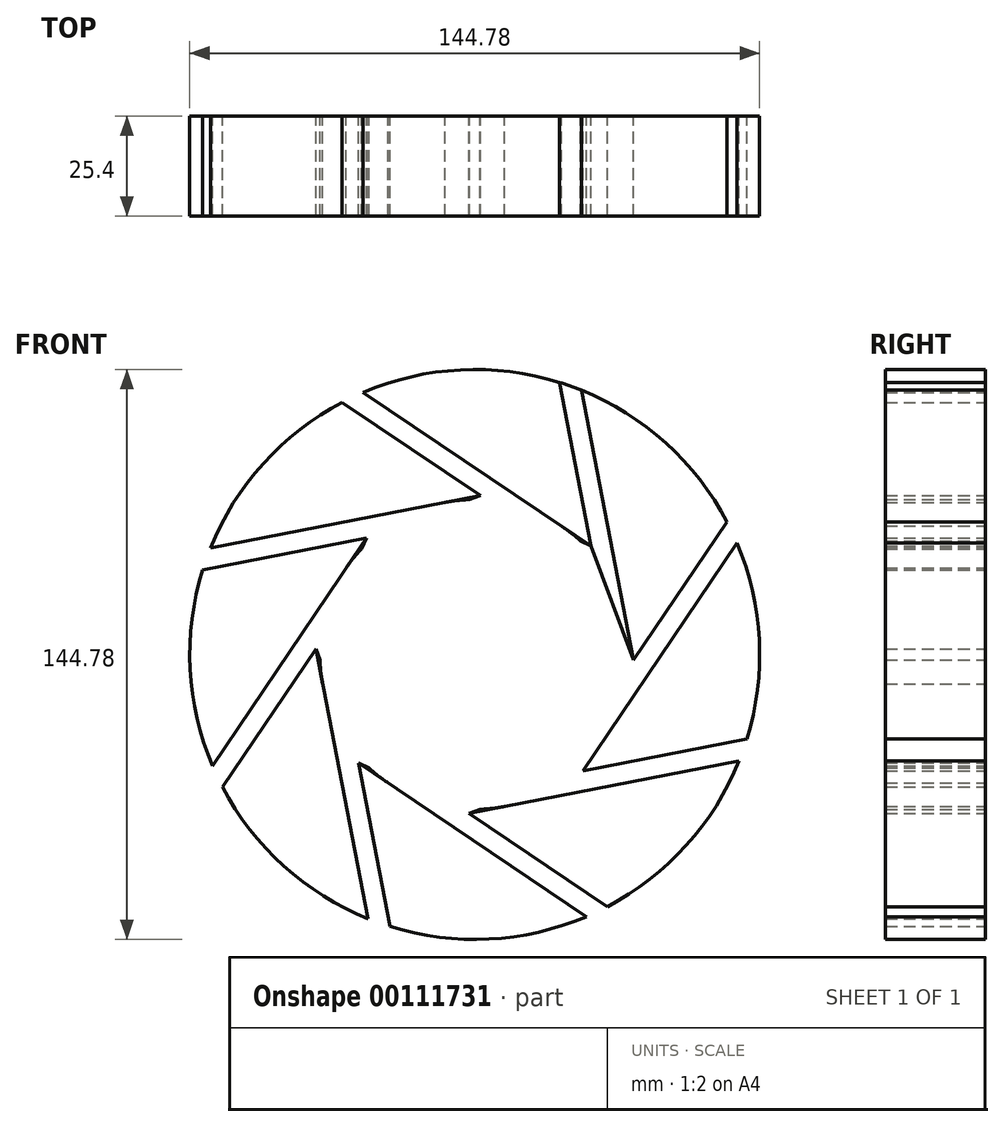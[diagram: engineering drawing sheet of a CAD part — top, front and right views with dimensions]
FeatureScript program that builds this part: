
annotation { "Feature Type Name" : "Feature", "Feature Type Description" : "" }
export const myFeature = defineFeature(function(context is Context, id is Id, definition is map)
    precondition{}
    {
        {
            var Q0;
            Q0=qCreatedBy(makeId("Front.planeOp"),FACE);
            var sketch = newSketch(context, id + "F0", { "sketchPlane" : qUnion([Q0])});
            skCircle(sketch, "E0", {"center": v(0, 0) * mm, "radius": 39.37 * mm});
            skCircle(sketch, "E1", {"center": v(0, 0) * mm, "radius": 72.4 * mm});
            skLineSegment(sketch, "E2", {"start": v(-67.14, 27.06) * mm, "end": v(1.42, 40.38) * mm});
            skLineSegment(sketch, "E3", {"start": v(1.42, 40.38) * mm, "end": v(-33.7, 64.07) * mm});
            skLineSegment(sketch, "E4.1.0", {"start": v(-66.6, -28.35) * mm, "end": v(-27.55, 29.56) * mm});
            skLineSegment(sketch, "E4.1.1", {"start": v(-27.55, 29.56) * mm, "end": v(-69.13, 21.48) * mm});
            skLineSegment(sketch, "E4.2.0", {"start": v(-27.06, -67.14) * mm, "end": v(-40.38, 1.42) * mm});
            skLineSegment(sketch, "E4.2.1", {"start": v(-40.38, 1.42) * mm, "end": v(-64.07, -33.7) * mm});
            skLineSegment(sketch, "E4.3.0", {"start": v(28.35, -66.6) * mm, "end": v(-29.56, -27.55) * mm});
            skLineSegment(sketch, "E4.3.1", {"start": v(-29.56, -27.55) * mm, "end": v(-21.48, -69.13) * mm});
            skLineSegment(sketch, "E4.4.0", {"start": v(67.14, -27.06) * mm, "end": v(-1.42, -40.38) * mm});
            skLineSegment(sketch, "E4.4.1", {"start": v(-1.42, -40.38) * mm, "end": v(33.7, -64.07) * mm});
            skLineSegment(sketch, "E4.5.0", {"start": v(66.6, 28.35) * mm, "end": v(27.55, -29.56) * mm});
            skLineSegment(sketch, "E4.5.1", {"start": v(27.55, -29.56) * mm, "end": v(69.13, -21.48) * mm});
            skLineSegment(sketch, "E4.6.0", {"start": v(27.06, 67.14) * mm, "end": v(40.38, -1.42) * mm});
            skLineSegment(sketch, "E4.6.1", {"start": v(40.38, -1.42) * mm, "end": v(64.07, 33.7) * mm});
            skLineSegment(sketch, "E4.7.0", {"start": v(-28.35, 66.6) * mm, "end": v(29.56, 27.55) * mm});
            skLineSegment(sketch, "E4.7.1", {"start": v(29.56, 27.55) * mm, "end": v(21.48, 69.13) * mm});
            skCircle(sketch, "E5.cCircle", {"center": v(0, 0) * mm, "radius": 40.4 * mm, "construction": true});
            skLineSegment(sketch, "E5.0", {"start": v(1.42, 40.38) * mm, "end": v(29.56, 27.55) * mm});
            skLineSegment(sketch, "E5.1", {"start": v(29.56, 27.55) * mm, "end": v(40.38, -1.42) * mm});
            skLineSegment(sketch, "E5.2", {"start": v(40.38, -1.42) * mm, "end": v(27.55, -29.56) * mm});
            skLineSegment(sketch, "E5.3", {"start": v(27.55, -29.56) * mm, "end": v(-1.42, -40.38) * mm});
            skLineSegment(sketch, "E5.4", {"start": v(-1.42, -40.38) * mm, "end": v(-29.56, -27.55) * mm});
            skLineSegment(sketch, "E5.5", {"start": v(-29.56, -27.55) * mm, "end": v(-40.38, 1.42) * mm});
            skLineSegment(sketch, "E5.6", {"start": v(-40.38, 1.42) * mm, "end": v(-27.55, 29.56) * mm});
            skLineSegment(sketch, "E5.7", {"start": v(-27.55, 29.56) * mm, "end": v(1.42, 40.38) * mm});
            skSolve(sketch);
        }
        {
            var Q0;
            {var subQ3=sQuery(id+"F0.wireOp",EDGE,"E3");Q0=makeQuery(id+"F0.imprint","IMPRINT",FACE,{"disambiguationData":[TD([[makeQuery(id+"F0.imprint","IMPRINT",EDGE,{"derivedFrom":subQ3}),1.0]])]});}
            var Q1;
            {var subQ3=sQuery(id+"F0.wireOp",EDGE,"E4.7.1");Q1=makeQuery(id+"F0.imprint","IMPRINT",FACE,{"disambiguationData":[TD([[makeQuery(id+"F0.imprint","IMPRINT",EDGE,{"derivedFrom":subQ3}),1.0]])]});}
            var Q2;
            {var subQ3=sQuery(id+"F0.wireOp",EDGE,"E4.6.1");Q2=makeQuery(id+"F0.imprint","IMPRINT",FACE,{"disambiguationData":[TD([[makeQuery(id+"F0.imprint","IMPRINT",EDGE,{"derivedFrom":subQ3}),1.0]])]});}
            var Q3;
            {var subQ3=sQuery(id+"F0.wireOp",EDGE,"E4.5.1");Q3=makeQuery(id+"F0.imprint","IMPRINT",FACE,{"disambiguationData":[TD([[makeQuery(id+"F0.imprint","IMPRINT",EDGE,{"derivedFrom":subQ3}),1.0]])]});}
            var Q4;
            {var subQ3=sQuery(id+"F0.wireOp",EDGE,"E4.4.1");Q4=makeQuery(id+"F0.imprint","IMPRINT",FACE,{"disambiguationData":[TD([[makeQuery(id+"F0.imprint","IMPRINT",EDGE,{"derivedFrom":subQ3}),1.0]])]});}
            var Q5;
            {var subQ3=sQuery(id+"F0.wireOp",EDGE,"E4.3.1");Q5=makeQuery(id+"F0.imprint","IMPRINT",FACE,{"disambiguationData":[TD([[makeQuery(id+"F0.imprint","IMPRINT",EDGE,{"derivedFrom":subQ3}),1.0]])]});}
            var Q6;
            {var subQ3=sQuery(id+"F0.wireOp",EDGE,"E4.2.1");Q6=makeQuery(id+"F0.imprint","IMPRINT",FACE,{"disambiguationData":[TD([[makeQuery(id+"F0.imprint","IMPRINT",EDGE,{"derivedFrom":subQ3}),1.0]])]});}
            var Q7;
            {var subQ3=sQuery(id+"F0.wireOp",EDGE,"E4.1.1");Q7=makeQuery(id+"F0.imprint","IMPRINT",FACE,{"disambiguationData":[TD([[makeQuery(id+"F0.imprint","IMPRINT",EDGE,{"derivedFrom":subQ3}),1.0]])]});}
            extrude(context, id + "F1", {"entities" : qUnion([Q0, Q1, Q2, Q3, Q4, Q5, Q6, Q7]), "endBound" : BoundingType.SYMMETRIC, "depth" : 25.4 * mm});
        }
        {
            var Q0;
            {var subQ0=sQuery(id+"F0.wireOp",EDGE,"E5.0");var subQ1=sQuery(id+"F0.wireOp",EDGE,"E0");var subQ2=makeQuery(id+"F0.imprint","INTERSECT",VERTEX,{"disambiguationData":[OD(1.0)],"derivedFrom":[subQ1,subQ0]});Q0=makeQuery(id+"F0.imprint","IMPRINT",FACE,{"disambiguationData":[TD([[makeQuery(id+"F0.imprint","IMPRINT",EDGE,{"disambiguationData":[TD([[subQ2,-1.0]])],"derivedFrom":subQ1}),-1.0]])]});}
            var Q1;
            {var subQ0=sQuery(id+"F0.wireOp",EDGE,"E5.7");var subQ1=sQuery(id+"F0.wireOp",EDGE,"E0");var subQ2=makeQuery(id+"F0.imprint","INTERSECT",VERTEX,{"disambiguationData":[OD(1.0)],"derivedFrom":[subQ1,subQ0]});Q1=makeQuery(id+"F0.imprint","IMPRINT",FACE,{"disambiguationData":[TD([[makeQuery(id+"F0.imprint","IMPRINT",EDGE,{"disambiguationData":[TD([[subQ2,-1.0]])],"derivedFrom":subQ1}),-1.0]])]});}
            var Q2;
            {var subQ0=sQuery(id+"F0.wireOp",EDGE,"E5.6");var subQ1=sQuery(id+"F0.wireOp",EDGE,"E0");var subQ2=makeQuery(id+"F0.imprint","INTERSECT",VERTEX,{"disambiguationData":[OD(1.0)],"derivedFrom":[subQ1,subQ0]});Q2=makeQuery(id+"F0.imprint","IMPRINT",FACE,{"disambiguationData":[TD([[makeQuery(id+"F0.imprint","IMPRINT",EDGE,{"disambiguationData":[TD([[subQ2,-1.0]])],"derivedFrom":subQ1}),-1.0]])]});}
            var Q3;
            {var subQ0=sQuery(id+"F0.wireOp",EDGE,"E5.1");var subQ1=sQuery(id+"F0.wireOp",EDGE,"E0");var subQ2=makeQuery(id+"F0.imprint","INTERSECT",VERTEX,{"disambiguationData":[OD(1.0)],"derivedFrom":[subQ1,subQ0]});Q3=makeQuery(id+"F0.imprint","IMPRINT",FACE,{"disambiguationData":[TD([[makeQuery(id+"F0.imprint","IMPRINT",EDGE,{"disambiguationData":[TD([[subQ2,-1.0]])],"derivedFrom":subQ1}),-1.0]])]});}
            var Q4;
            {var subQ0=sQuery(id+"F0.wireOp",EDGE,"E5.1");var subQ1=sQuery(id+"F0.wireOp",EDGE,"E0");var subQ2=makeQuery(id+"F0.imprint","INTERSECT",VERTEX,{"disambiguationData":[OD(0.0)],"derivedFrom":[subQ1,subQ0]});Q4=makeQuery(id+"F0.imprint","IMPRINT",FACE,{"disambiguationData":[TD([[makeQuery(id+"F0.imprint","IMPRINT",EDGE,{"disambiguationData":[TD([[subQ2,1.0]])],"derivedFrom":subQ1}),-1.0]])]});}
            var Q5;
            {var subQ0=sQuery(id+"F0.wireOp",EDGE,"E5.3");var subQ1=sQuery(id+"F0.wireOp",EDGE,"E0");var subQ2=makeQuery(id+"F0.imprint","INTERSECT",VERTEX,{"disambiguationData":[OD(1.0)],"derivedFrom":[subQ1,subQ0]});Q5=makeQuery(id+"F0.imprint","IMPRINT",FACE,{"disambiguationData":[TD([[makeQuery(id+"F0.imprint","IMPRINT",EDGE,{"disambiguationData":[TD([[subQ2,-1.0]])],"derivedFrom":subQ1}),-1.0]])]});}
            var Q6;
            {var subQ0=sQuery(id+"F0.wireOp",EDGE,"E5.4");var subQ1=sQuery(id+"F0.wireOp",EDGE,"E0");var subQ2=makeQuery(id+"F0.imprint","INTERSECT",VERTEX,{"disambiguationData":[OD(1.0)],"derivedFrom":[subQ1,subQ0]});Q6=makeQuery(id+"F0.imprint","IMPRINT",FACE,{"disambiguationData":[TD([[makeQuery(id+"F0.imprint","IMPRINT",EDGE,{"disambiguationData":[TD([[subQ2,-1.0]])],"derivedFrom":subQ1}),-1.0]])]});}
            var Q7;
            {var subQ0=sQuery(id+"F0.wireOp",EDGE,"E5.1");var subQ1=sQuery(id+"F0.wireOp",EDGE,"E0");var subQ5=makeQuery(id+"F0.imprint","INTERSECT",VERTEX,{"disambiguationData":[OD(1.0)],"derivedFrom":[subQ1,subQ0]});Q7=makeQuery(id+"F0.imprint","IMPRINT",FACE,{"disambiguationData":[TD([[makeQuery(id+"F0.imprint","IMPRINT",EDGE,{"disambiguationData":[TD([[subQ5,-1.0]])],"derivedFrom":subQ1}),1.0]])]});}
            var Q8;
            {var subQ0=sQuery(id+"F0.wireOp",EDGE,"E5.5");var subQ1=sQuery(id+"F0.wireOp",EDGE,"E0");var subQ2=makeQuery(id+"F0.imprint","INTERSECT",VERTEX,{"disambiguationData":[OD(1.0)],"derivedFrom":[subQ1,subQ0]});Q8=makeQuery(id+"F0.imprint","IMPRINT",FACE,{"disambiguationData":[TD([[makeQuery(id+"F0.imprint","IMPRINT",EDGE,{"disambiguationData":[TD([[subQ2,-1.0]])],"derivedFrom":subQ1}),-1.0]])]});}
            extrude(context, id + "F2", {"entities" : qUnion([Q0, Q1, Q2, Q3, Q4, Q5, Q6, Q7, Q8]), "endBound" : BoundingType.SYMMETRIC, "depth" : 25.4 * mm});
        }
    });
